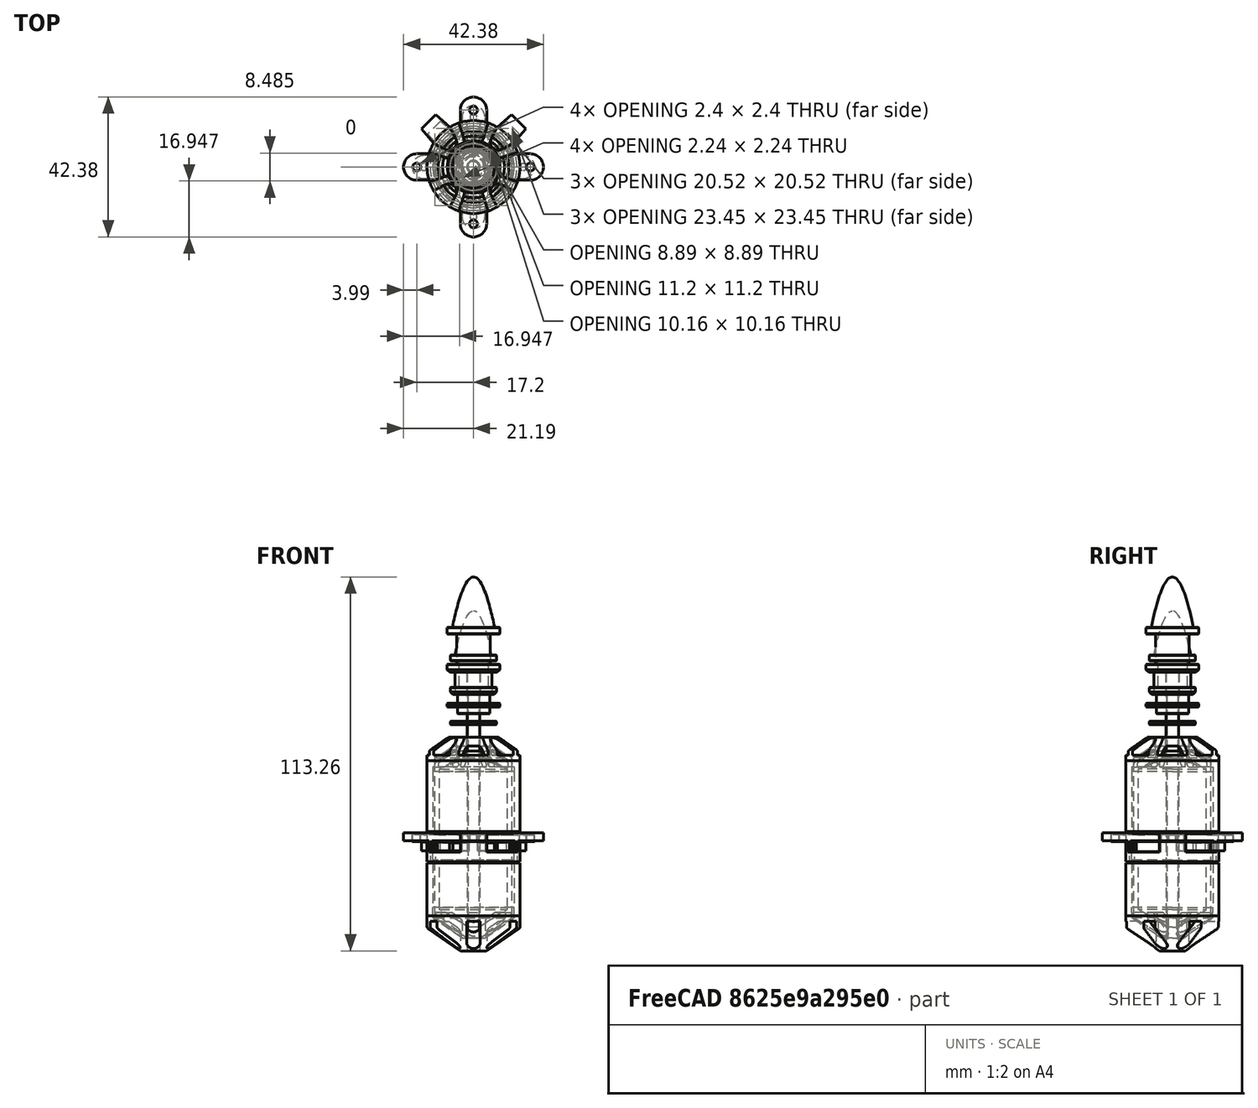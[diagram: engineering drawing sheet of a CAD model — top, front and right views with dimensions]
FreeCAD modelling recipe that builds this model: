
FCSTD DOCUMENT  (FreeCAD 0.19R24291 (Git))
Label: HimaxCR2805
License: All rights reserved
LicenseURL: http://en.wikipedia.org/wiki/All_rights_reserved
objects: Part::FeaturePython×3, Part::Feature×1
note: 4 computed .brp shape members not serialized (recipe doc carries the construction recipe); baked Part::Feature solids carry a one-line shape summary decoded from their .brp

FEATURE [Part::Feature] Part__Feature  label="Himax CR3516 Contra-Rotating Motor"
  Placement = pos=(0,0,6) rot=(0,0,1;0rad)
  shape: bbox 52.98 x 52.98 x 141.6 mm, 231 faces, 9 solids (baked)
FEATURE [Part::FeaturePython] Clone  label="Himax CR3516 Contra-Rotating Motor001"  # Draft clone (typed FeaturePython)
  AttacherType = Attacher::AttachEngine3D
  Fuse = false
  Objects = -> [Part__Feature]
  Placement = pos=(0,0,6) rot=(0,0,1;0rad)
  Scale = (1,1,1)
FEATURE [Part::FeaturePython] Clone001  label="Himax CR3516 Contra-Rotating Motor002"  # Draft clone (typed FeaturePython)
  AttacherType = Attacher::AttachEngine3D
  Fuse = false
  Objects = -> [Clone]
  Placement = pos=(0,0,4.2) rot=(0,0,1;0rad)
  Scale = (0.7,0.7,0.7)
FEATURE [Part::FeaturePython] Clone002  label="Himax CR3516 Contra-Rotating Motor003"  # Draft clone (typed FeaturePython)
  AttacherType = Attacher::AttachEngine3D
  Fuse = false
  Objects = -> [Clone]
  Placement = pos=(0,0,4.8) rot=(0,0,1;0rad)
  Scale = (0.8,0.8,0.8)
